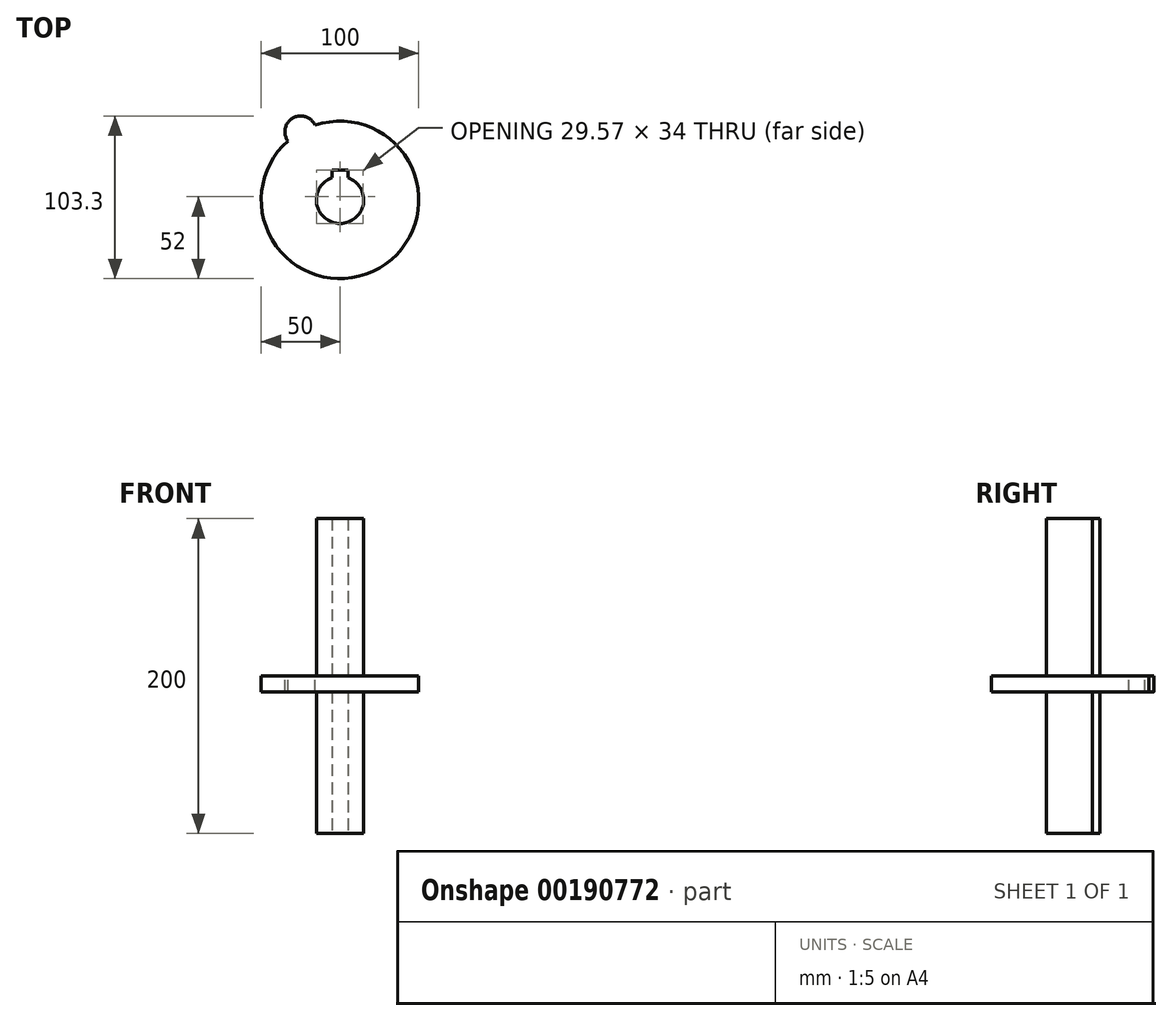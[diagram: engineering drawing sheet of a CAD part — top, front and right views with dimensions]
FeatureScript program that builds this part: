
annotation { "Feature Type Name" : "Feature", "Feature Type Description" : "" }
export const myFeature = defineFeature(function(context is Context, id is Id, definition is map)
    precondition{}
    {
        {
            var Q0;
            Q0=qCreatedBy(makeId("Top.planeOp"),FACE);
            var sketch = newSketch(context, id + "F0", { "sketchPlane" : qUnion([Q0])});
            skArc(sketch, "E0", {"start": v(-33.12, 37.46) * mm, "mid": v(25, -43.3) * mm, "end": v(-15.88, 47.41) * mm});
            skArc(sketch, "E1", {"start": v(-15.88, 47.41) * mm, "mid": v(-30, 51.96) * mm, "end": v(-33.12, 37.46) * mm});
            skLineSegment(sketch, "E2", {"start": v(-25, 43.3) * mm, "end": v(0, 0) * mm});
            skLineSegment(sketch, "E3", {"start": v(0, 0) * mm, "end": v(0, 50) * mm});
            skSolve(sketch);
        }
        {
            var Q0;
            Q0 = qSketchRegion(id + "F0", true);
            extrude(context, id + "F1", {"entities" : qUnion([Q0]), "endBound" : BoundingType.SYMMETRIC, "oppositeDirection" : true, "depth" : 10 * mm});
        }
        {
            var Q0;
            Q0=makeQuery(id+"F1.opExtrude","CAP_FACE",FACE,{"disambiguationData":[OSD([sQuery(id+"F0.wireOp",EDGE,"E0"),sQuery(id+"F0.wireOp",EDGE,"E1")])],"isStart":true});
            var sketch = newSketch(context, id + "F2", { "sketchPlane" : qUnion([Q0])});
            skCircle(sketch, "E4", {"center": v(0, 0) * mm, "radius": 15 * mm});
            skLineSegment(sketch, "E5.bottom", {"start": v(-5, 19) * mm, "end": v(5, 19) * mm});
            skLineSegment(sketch, "E5.top", {"start": v(-5, 11) * mm, "end": v(5, 11) * mm});
            skLineSegment(sketch, "E5.left", {"start": v(-5, 19) * mm, "end": v(-5, 11) * mm});
            skLineSegment(sketch, "E5.right", {"start": v(5, 19) * mm, "end": v(5, 11) * mm});
            skPoint(sketch, "E5.middle", {"position": v(0, 15) * mm});
            skSolve(sketch);
        }
        {
            var Q0;
            Q0 = qSketchRegion(id + "F2", true);
            extrude(context, id + "F3", {"entities" : qUnion([Q0]), "operationType" : NewBodyOperationType.ADD, "endBound" : BoundingType.SYMMETRIC, "depth" : 200 * mm});
        }
    });
